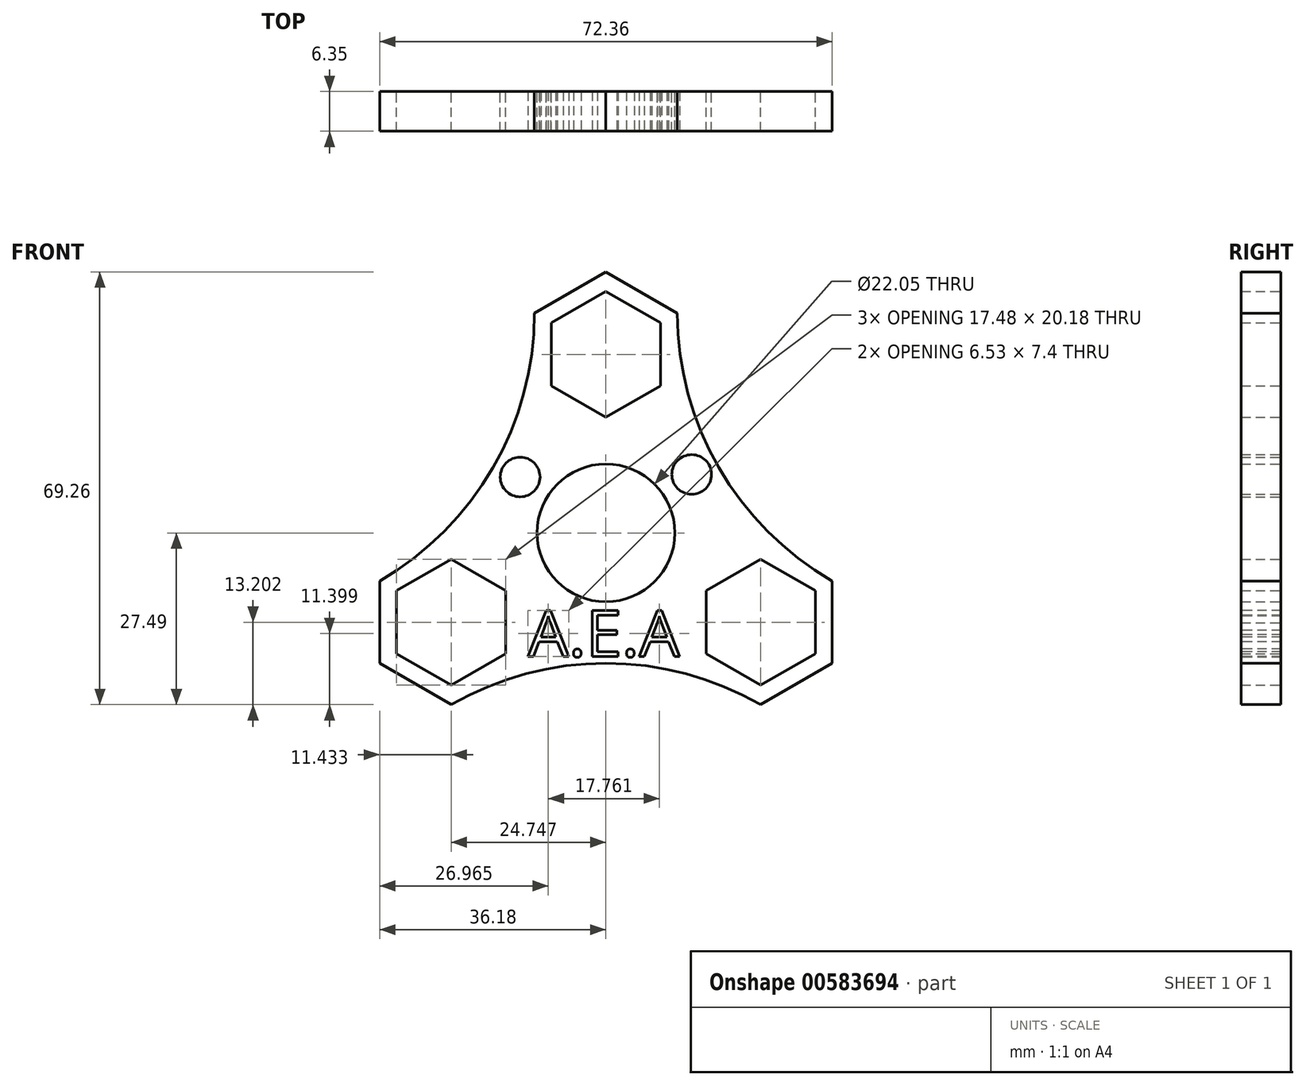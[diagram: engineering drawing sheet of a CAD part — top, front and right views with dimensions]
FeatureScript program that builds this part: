
annotation { "Feature Type Name" : "Feature", "Feature Type Description" : "" }
export const myFeature = defineFeature(function(context is Context, id is Id, definition is map)
    precondition{}
    {
        {
            var Q0;
            Q0=qCreatedBy(makeId("Front.planeOp"),FACE);
            var sketch = newSketch(context, id + "F0", { "sketchPlane" : qUnion([Q0])});
            skCircle(sketch, "E0", {"center": v(0, 0) * mm, "radius": 11.02 * mm});
            skCircle(sketch, "E1", {"center": v(0, 0) * mm, "radius": 14.29 * mm});
            skCircle(sketch, "E2.cCircle", {"center": v(0, 28.58) * mm, "radius": 8.74 * mm, "construction": true});
            skLineSegment(sketch, "E2.0", {"start": v(-8.74, 23.53) * mm, "end": v(-8.74, 33.62) * mm});
            skLineSegment(sketch, "E2.1", {"start": v(-8.74, 33.62) * mm, "end": v(0, 38.66) * mm});
            skLineSegment(sketch, "E2.2", {"start": v(0, 38.66) * mm, "end": v(8.74, 33.62) * mm});
            skLineSegment(sketch, "E2.3", {"start": v(8.74, 33.62) * mm, "end": v(8.74, 23.53) * mm});
            skLineSegment(sketch, "E2.4", {"start": v(8.74, 23.53) * mm, "end": v(0, 18.49) * mm});
            skLineSegment(sketch, "E2.5", {"start": v(0, 18.49) * mm, "end": v(-8.74, 23.53) * mm});
            skPoint(sketch, "E2.0.midPoint", {"position": v(-8.74, 28.58) * mm});
            skCircle(sketch, "E3.cCircle", {"center": v(0, 28.58) * mm, "radius": 11.43 * mm, "construction": true});
            skLineSegment(sketch, "E3.0", {"start": v(-11.43, 21.98) * mm, "end": v(-11.43, 35.17) * mm});
            skLineSegment(sketch, "E3.1", {"start": v(-11.43, 35.17) * mm, "end": v(0, 41.77) * mm});
            skLineSegment(sketch, "E3.2", {"start": v(0, 41.77) * mm, "end": v(11.43, 35.17) * mm});
            skLineSegment(sketch, "E3.3", {"start": v(11.43, 35.17) * mm, "end": v(11.43, 21.98) * mm});
            skLineSegment(sketch, "E3.4", {"start": v(11.43, 21.98) * mm, "end": v(0, 15.38) * mm});
            skLineSegment(sketch, "E3.5", {"start": v(0, 15.38) * mm, "end": v(-11.43, 21.98) * mm});
            skPoint(sketch, "E3.0.midPoint", {"position": v(-11.43, 28.58) * mm});
            skLineSegment(sketch, "E4.1.0", {"start": v(-24.75, -1.09) * mm, "end": v(-13.32, -7.69) * mm});
            skLineSegment(sketch, "E4.1.1", {"start": v(-24.75, -24.38) * mm, "end": v(-33.48, -19.33) * mm});
            skLineSegment(sketch, "E4.1.2", {"start": v(-13.32, -7.69) * mm, "end": v(-13.32, -20.89) * mm});
            skLineSegment(sketch, "E4.1.3", {"start": v(-24.75, -4.2) * mm, "end": v(-16, -9.24) * mm});
            skCircle(sketch, "E4.1.4", {"center": v(-24.75, -14.29) * mm, "radius": 8.74 * mm, "construction": true});
            skLineSegment(sketch, "E4.1.5", {"start": v(-33.48, -19.33) * mm, "end": v(-33.48, -9.24) * mm});
            skCircle(sketch, "E4.1.6", {"center": v(-24.75, -14.29) * mm, "radius": 11.43 * mm, "construction": true});
            skLineSegment(sketch, "E4.1.7", {"start": v(-13.32, -20.89) * mm, "end": v(-24.75, -27.49) * mm});
            skLineSegment(sketch, "E4.1.8", {"start": v(-24.75, -27.49) * mm, "end": v(-36.18, -20.89) * mm});
            skPoint(sketch, "E4.1.9", {"position": v(-19.03, -24.19) * mm});
            skLineSegment(sketch, "E4.1.10", {"start": v(-16, -9.24) * mm, "end": v(-16, -19.33) * mm});
            skLineSegment(sketch, "E4.1.11", {"start": v(-36.18, -20.89) * mm, "end": v(-36.18, -7.69) * mm});
            skLineSegment(sketch, "E4.1.12", {"start": v(-36.18, -7.69) * mm, "end": v(-24.75, -1.09) * mm});
            skPoint(sketch, "E4.1.13", {"position": v(-20.38, -21.85) * mm});
            skLineSegment(sketch, "E4.1.14", {"start": v(-16, -19.33) * mm, "end": v(-24.75, -24.38) * mm});
            skLineSegment(sketch, "E4.1.15", {"start": v(-33.48, -9.24) * mm, "end": v(-24.75, -4.2) * mm});
            skLineSegment(sketch, "E4.2.0", {"start": v(13.32, -20.89) * mm, "end": v(13.32, -7.69) * mm});
            skLineSegment(sketch, "E4.2.1", {"start": v(33.48, -9.24) * mm, "end": v(33.48, -19.33) * mm});
            skLineSegment(sketch, "E4.2.2", {"start": v(13.32, -7.69) * mm, "end": v(24.75, -1.09) * mm});
            skLineSegment(sketch, "E4.2.3", {"start": v(16, -19.33) * mm, "end": v(16, -9.24) * mm});
            skCircle(sketch, "E4.2.4", {"center": v(24.75, -14.29) * mm, "radius": 8.74 * mm, "construction": true});
            skLineSegment(sketch, "E4.2.5", {"start": v(33.48, -19.33) * mm, "end": v(24.75, -24.38) * mm});
            skCircle(sketch, "E4.2.6", {"center": v(24.75, -14.29) * mm, "radius": 11.43 * mm, "construction": true});
            skLineSegment(sketch, "E4.2.7", {"start": v(24.75, -1.09) * mm, "end": v(36.18, -7.69) * mm});
            skLineSegment(sketch, "E4.2.8", {"start": v(36.18, -7.69) * mm, "end": v(36.18, -20.89) * mm});
            skPoint(sketch, "E4.2.9", {"position": v(30.46, -4.39) * mm});
            skLineSegment(sketch, "E4.2.10", {"start": v(16, -9.24) * mm, "end": v(24.75, -4.2) * mm});
            skLineSegment(sketch, "E4.2.11", {"start": v(36.18, -20.89) * mm, "end": v(24.75, -27.49) * mm});
            skLineSegment(sketch, "E4.2.12", {"start": v(24.75, -27.49) * mm, "end": v(13.32, -20.89) * mm});
            skPoint(sketch, "E4.2.13", {"position": v(29.12, -6.72) * mm});
            skLineSegment(sketch, "E4.2.14", {"start": v(24.75, -4.2) * mm, "end": v(33.48, -9.24) * mm});
            skLineSegment(sketch, "E4.2.15", {"start": v(24.75, -24.38) * mm, "end": v(16, -19.33) * mm});
            skArc(sketch, "E5", {"start": v(-36.18, -7.69) * mm, "mid": v(-18.06, 10.43) * mm, "end": v(-11.43, 35.17) * mm});
            skArc(sketch, "E6", {"start": v(11.43, 35.17) * mm, "mid": v(18.06, 10.43) * mm, "end": v(36.18, -7.69) * mm});
            skArc(sketch, "E7", {"start": v(24.75, -27.49) * mm, "mid": v(0, -20.85) * mm, "end": v(-24.75, -27.49) * mm});
            skSolve(sketch);
        }
        {
            var Q0;
            Q0 = qSketchRegion(id + "F0", true);
            var Q1;
            Q1=makeQuery(id+"F0.imprint","IMPRINT",FACE,{"disambiguationData":[TD([[makeQuery(id+"F0.imprint","IMPRINT",EDGE,{"derivedFrom":sQuery(id+"F0.wireOp",EDGE,"E0")}),-1.0]])]});
            extrude(context, id + "F1", {"entities" : qUnion([Q0, Q1]), "depth" : 6.35 * mm, "offsetDistance" : 25.4 * mm});
        }
        {
            var Q0;
            Q0=qCreatedBy(makeId("Front.planeOp"),FACE);
            var sketch = newSketch(context, id + "F2", { "sketchPlane" : qUnion([Q0])});
            skText(sketch, "E8", { "text": "Abby", "fontName": "OpenSans-Regular.ttf"});
            const initialGuessF2  = {"E8": [-0.00756, -0.0199, 1, 0, 0.00672]};
            skSetInitialGuess(sketch, initialGuessF2);
            skSolve(sketch);
        }
        {
            var Q0;
            Q0 = qSketchRegion(id + "F2", true);
            extrude(context, id + "F3", {"entities" : qUnion([Q0]), "operationType" : NewBodyOperationType.REMOVE, "oppositeDirection" : true, "depth" : 25.4 * mm, "offsetDistance" : 25.4 * mm});
        }
        {
            var Q0;
            Q0=makeQuery(id+"F1.opExtrude","CAP_FACE",FACE,{"disambiguationData":[OSD([sQuery(id+"F0.wireOp",EDGE,"E0"),sQuery(id+"F0.wireOp",EDGE,"E2.0"),sQuery(id+"F0.wireOp",EDGE,"E2.1"),sQuery(id+"F0.wireOp",EDGE,"E2.2"),sQuery(id+"F0.wireOp",EDGE,"E2.3"),sQuery(id+"F0.wireOp",EDGE,"E2.4"),sQuery(id+"F0.wireOp",EDGE,"E2.5"),sQuery(id+"F0.wireOp",EDGE,"E3.1"),sQuery(id+"F0.wireOp",EDGE,"E3.2"),sQuery(id+"F0.wireOp",EDGE,"E4.1.1"),sQuery(id+"F0.wireOp",EDGE,"E4.1.3"),sQuery(id+"F0.wireOp",EDGE,"E4.1.5"),sQuery(id+"F0.wireOp",EDGE,"E4.1.8"),sQuery(id+"F0.wireOp",EDGE,"E4.1.10"),sQuery(id+"F0.wireOp",EDGE,"E4.1.11"),sQuery(id+"F0.wireOp",EDGE,"E4.1.14"),sQuery(id+"F0.wireOp",EDGE,"E4.1.15"),sQuery(id+"F0.wireOp",EDGE,"E4.2.1"),sQuery(id+"F0.wireOp",EDGE,"E4.2.3"),sQuery(id+"F0.wireOp",EDGE,"E4.2.5"),sQuery(id+"F0.wireOp",EDGE,"E4.2.8"),sQuery(id+"F0.wireOp",EDGE,"E4.2.10"),sQuery(id+"F0.wireOp",EDGE,"E4.2.11"),sQuery(id+"F0.wireOp",EDGE,"E4.2.14"),sQuery(id+"F0.wireOp",EDGE,"E4.2.15"),sQuery(id+"F0.wireOp",EDGE,"E5"),sQuery(id+"F0.wireOp",EDGE,"E6"),sQuery(id+"F0.wireOp",EDGE,"E7")])],"isStart":false});
            var sketch = newSketch(context, id + "F4", { "sketchPlane" : qUnion([Q0])});
            skText(sketch, "E9", { "text": "A.E.A", "fontName": "OpenSans-Regular.ttf"});
            const initialGuessF4  = {"E9": [-0.01248, -0.01979, 1, 0, 0.00743]};
            skSetInitialGuess(sketch, initialGuessF4);
            skSolve(sketch);
        }
        {
            var Q0;
            Q0 = qSketchRegion(id + "F4", true);
            extrude(context, id + "F5", {"entities" : qUnion([Q0]), "operationType" : NewBodyOperationType.REMOVE, "endBound" : BoundingType.THROUGH_ALL, "oppositeDirection" : true, "depth" : 25.4 * mm, "offsetDistance" : 25.4 * mm});
        }
        {
            var Q0;
            Q0=qCreatedBy(makeId("Front.planeOp"),FACE);
            var sketch = newSketch(context, id + "F6", { "sketchPlane" : qUnion([Q0])});
            skCircle(sketch, "E10", {"center": v(-13.72, 8.95) * mm, "radius": 3.18 * mm});
            skCircle(sketch, "E11", {"center": v(13.72, 9.35) * mm, "radius": 3.18 * mm});
            skSolve(sketch);
        }
        {
            var Q0;
            Q0 = qSketchRegion(id + "F6", true);
            extrude(context, id + "F7", {"entities" : qUnion([Q0]), "operationType" : NewBodyOperationType.REMOVE, "depth" : 25.4 * mm, "offsetDistance" : 25.4 * mm});
        }
    });
